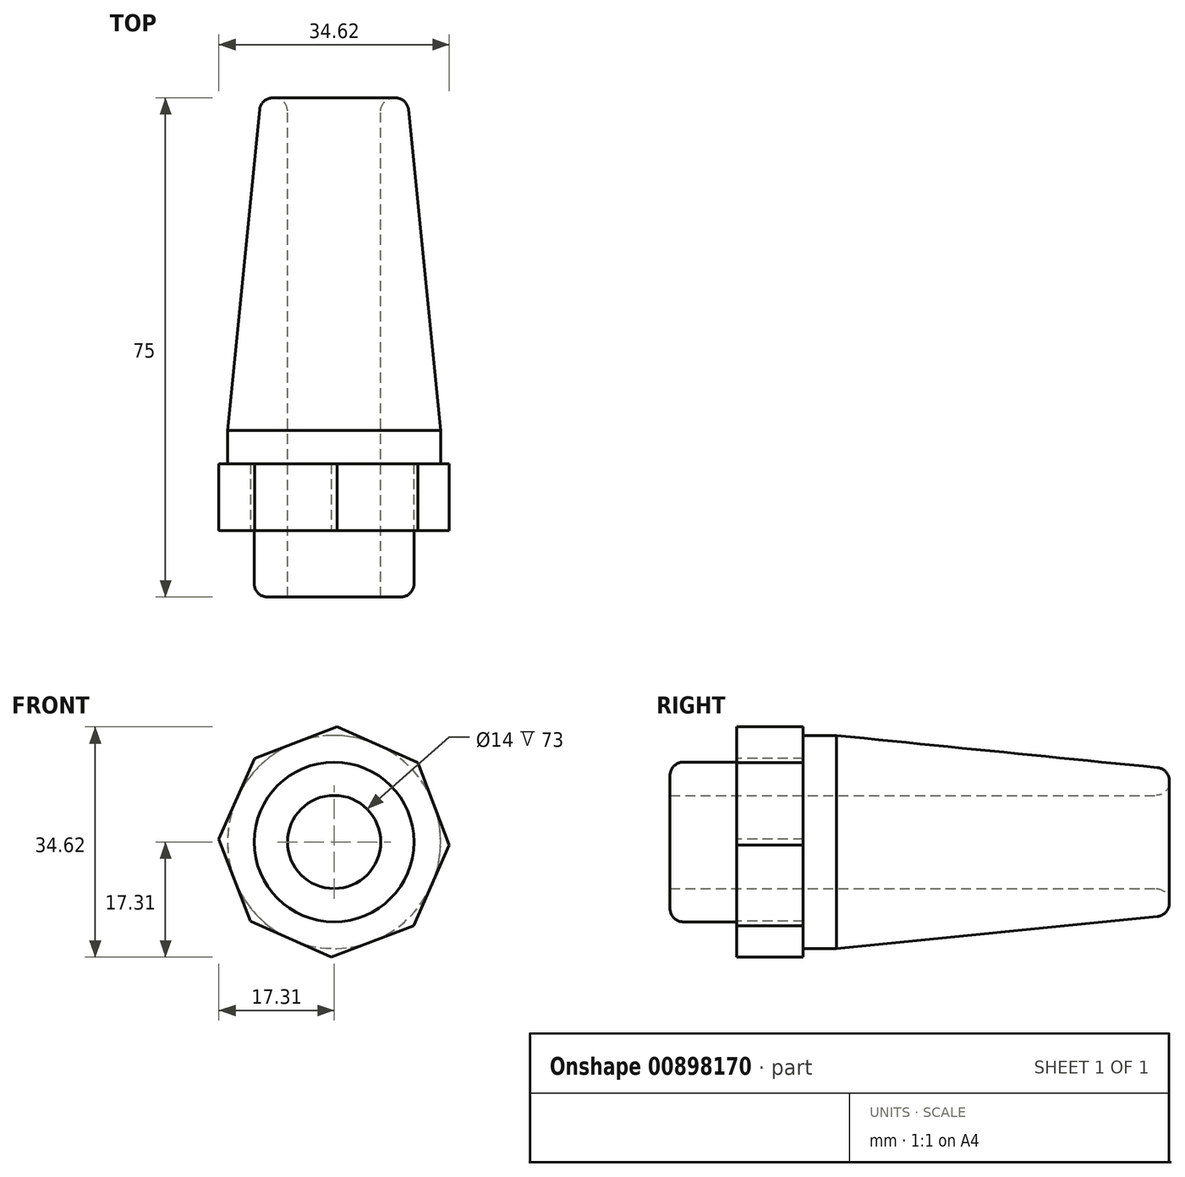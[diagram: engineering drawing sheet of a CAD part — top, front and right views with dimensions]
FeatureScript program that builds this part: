
annotation { "Feature Type Name" : "Feature", "Feature Type Description" : "" }
export const myFeature = defineFeature(function(context is Context, id is Id, definition is map)
    precondition{}
    {
        {
            var Q0;
            Q0=qCreatedBy(makeId("Front.planeOp"),FACE);
            var sketch = newSketch(context, id + "F0", { "sketchPlane" : qUnion([Q0])});
            skCircle(sketch, "E0", {"center": v(0, 0) * mm, "radius": 12 * mm});
            skCircle(sketch, "E1.cCircle", {"center": v(0, 0) * mm, "radius": 16 * mm, "construction": true});
            skLineSegment(sketch, "E1.0", {"start": v(12.56, 11.92) * mm, "end": v(17.31, -0.46) * mm});
            skLineSegment(sketch, "E1.1", {"start": v(17.31, -0.46) * mm, "end": v(11.92, -12.56) * mm});
            skLineSegment(sketch, "E1.2", {"start": v(11.92, -12.56) * mm, "end": v(-0.46, -17.31) * mm});
            skLineSegment(sketch, "E1.3", {"start": v(-0.46, -17.31) * mm, "end": v(-12.56, -11.92) * mm});
            skLineSegment(sketch, "E1.4", {"start": v(-12.56, -11.92) * mm, "end": v(-17.31, 0.46) * mm});
            skLineSegment(sketch, "E1.5", {"start": v(-17.31, 0.46) * mm, "end": v(-11.92, 12.56) * mm});
            skLineSegment(sketch, "E1.6", {"start": v(-11.92, 12.56) * mm, "end": v(0.46, 17.31) * mm});
            skLineSegment(sketch, "E1.7", {"start": v(0.46, 17.31) * mm, "end": v(12.56, 11.92) * mm});
            skPoint(sketch, "E1.0.midPoint", {"position": v(14.94, 5.73) * mm});
            skCircle(sketch, "E2", {"center": v(0, 0) * mm, "radius": 7 * mm});
            skSolve(sketch);
        }
        {
            var Q0;
            Q0=makeQuery(id+"F0.imprint","IMPRINT",FACE,{"disambiguationData":[TD([[makeQuery(id+"F0.imprint","IMPRINT",EDGE,{"derivedFrom":sQuery(id+"F0.wireOp",EDGE,"E0")}),1.0]])]});
            extrude(context, id + "F1", {"entities" : qUnion([Q0]), "depth" : 10 * mm, "offsetDistance" : 25 * mm});
        }
        {
            var Q0;
            Q0 = qSketchRegion(id + "F0", true);
            var Q1;
            Q1=makeQuery(id+"F1.opExtrude","CAP_FACE",FACE,{"disambiguationData":[OSD([sQuery(id+"F0.wireOp",EDGE,"E0"),sQuery(id+"F0.wireOp",EDGE,"E2")])],"isStart":true});
            extrude(context, id + "F2", {"entities" : qUnion([Q0, Q1]), "operationType" : NewBodyOperationType.ADD, "oppositeDirection" : true, "depth" : 10 * mm, "offsetDistance" : 25 * mm});
        }
        {
            var Q0;
            {var subQ0=sQuery(id+"F0.wireOp",EDGE,"E0");Q0=makeQuery(id+"F2.boolean.opBoolean","MERGE",FACE,{"derivedFrom":[makeQuery(id+"F2.opExtrude","CAP_FACE",FACE,{"disambiguationData":[OSD([subQ0,sQuery(id+"F0.wireOp",EDGE,"E1.0"),sQuery(id+"F0.wireOp",EDGE,"E1.1"),sQuery(id+"F0.wireOp",EDGE,"E1.2"),sQuery(id+"F0.wireOp",EDGE,"E1.3"),sQuery(id+"F0.wireOp",EDGE,"E1.4"),sQuery(id+"F0.wireOp",EDGE,"E1.5"),sQuery(id+"F0.wireOp",EDGE,"E1.6"),sQuery(id+"F0.wireOp",EDGE,"E1.7")])],"isStart":false}),makeQuery(id+"F2.opExtrude","CAP_FACE",FACE,{"disambiguationData":[OSD([subQ0,sQuery(id+"F0.wireOp",EDGE,"E2")])],"isStart":false})]});}
            var sketch = newSketch(context, id + "F3", { "sketchPlane" : qUnion([Q0])});
            skCircle(sketch, "E3", {"center": v(0, 0) * mm, "radius": 7 * mm});
            skCircle(sketch, "E4", {"center": v(0, 0) * mm, "radius": 16 * mm});
            skSolve(sketch);
        }
        {
            var Q0;
            Q0=makeQuery(id+"F3.imprint","IMPRINT",FACE,{"disambiguationData":[TD([[makeQuery(id+"F3.imprint","IMPRINT",EDGE,{"derivedFrom":sQuery(id+"F3.wireOp",EDGE,"E3")}),1.0]])]});
            extrude(context, id + "F4", {"entities" : qUnion([Q0]), "operationType" : NewBodyOperationType.ADD, "depth" : 55 * mm, "offsetDistance" : 25 * mm});
        }
        {
            var Q0;
            Q0=makeQuery(id+"F4.opExtrude","CAP_EDGE",EDGE,{"disambiguationData":[OSD([sQuery(id+"F3.wireOp",EDGE,"E4")])],"isStart":false});
            chamfer(context, id + "F5", {"entities" : qUnion([Q0]), "chamferType" : ChamferType.TWO_OFFSETS, "width1" : 5 * mm, "oppositeDirection" : false, "width2" : 50 * mm, "tangentPropagation" : true});
        }
        {
            var Q0;
            Q0=makeQuery(id+"F4.opExtrude","CAP_FACE",FACE,{"disambiguationData":[OSD([sQuery(id+"F3.wireOp",EDGE,"E3"),sQuery(id+"F3.wireOp",EDGE,"E4")])],"isStart":false});
            var Q1;
            Q1=makeQuery(id+"F1.opExtrude","CAP_EDGE",EDGE,{"disambiguationData":[OSD([sQuery(id+"F0.wireOp",EDGE,"E0")])],"isStart":false});
            fillet(context, id + "F6", {"entities" : qUnion([Q0, Q1]), "radius" : 2 * mm, "tangentPropagation" : true, "allowEdgeOverflow" : false});
        }
    });
